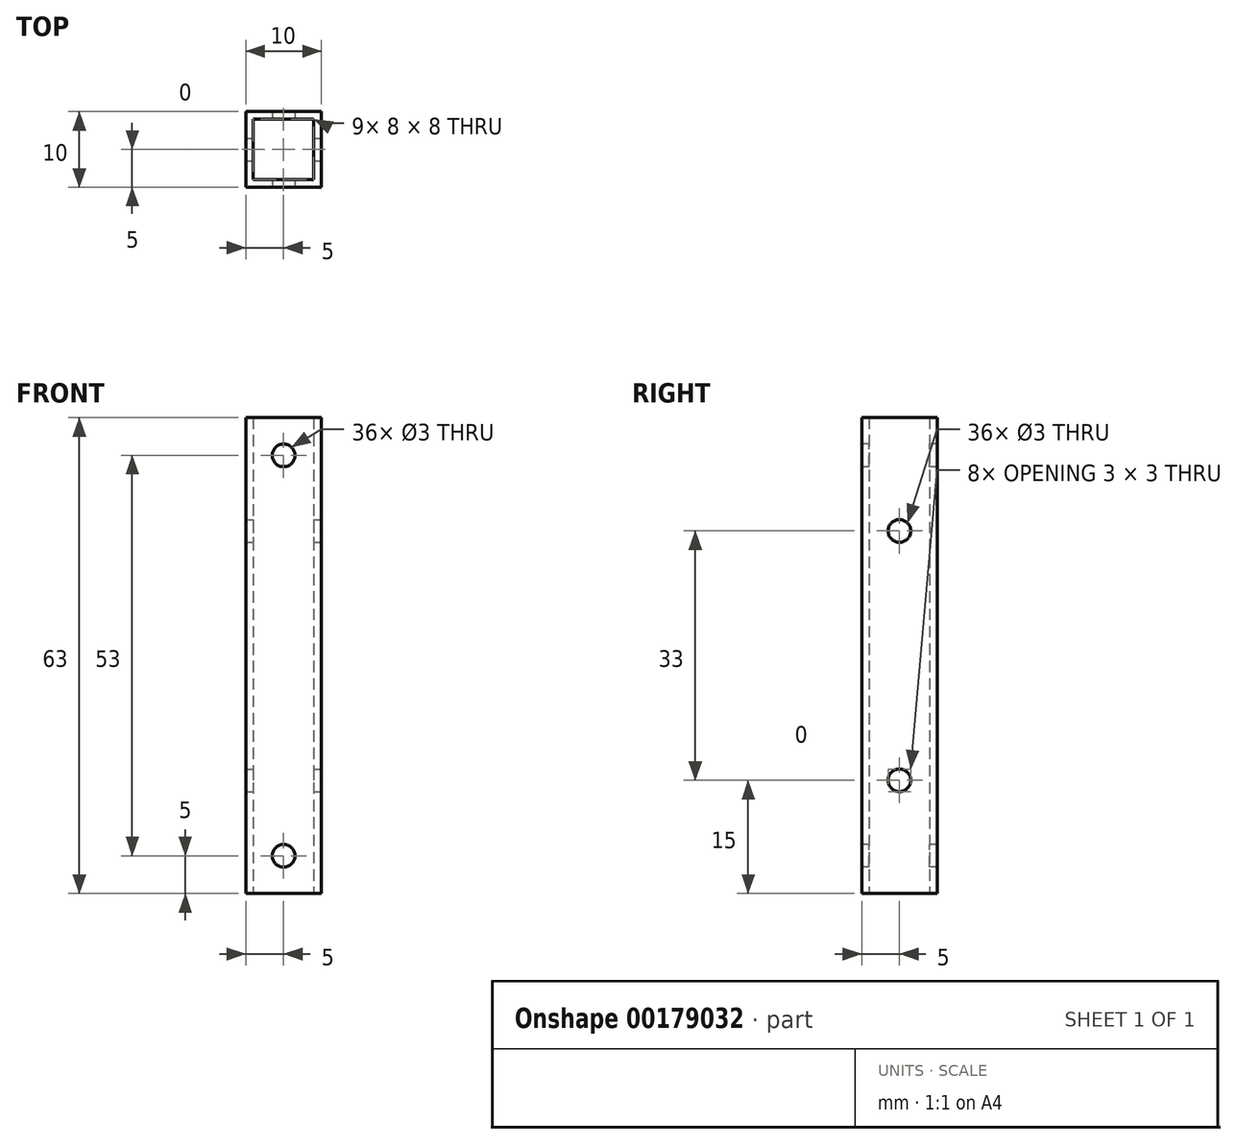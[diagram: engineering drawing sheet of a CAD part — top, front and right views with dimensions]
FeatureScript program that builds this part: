
annotation { "Feature Type Name" : "Feature", "Feature Type Description" : "" }
export const myFeature = defineFeature(function(context is Context, id is Id, definition is map)
    precondition{}
    {
        {
            var Q0;
            Q0=qCreatedBy(makeId("Top.planeOp"),FACE);
            var sketch = newSketch(context, id + "F0", { "sketchPlane" : qUnion([Q0])});
            skLineSegment(sketch, "E0.bottom", {"start": v(5, -5) * mm, "end": v(-5, -5) * mm});
            skLineSegment(sketch, "E0.top", {"start": v(5, 5) * mm, "end": v(-5, 5) * mm});
            skLineSegment(sketch, "E0.left", {"start": v(5, -5) * mm, "end": v(5, 5) * mm});
            skLineSegment(sketch, "E0.right", {"start": v(-5, -5) * mm, "end": v(-5, 5) * mm});
            skPoint(sketch, "E0.middle", {"position": v(0, 0) * mm});
            skLineSegment(sketch, "E1.bottom", {"start": v(4, -4) * mm, "end": v(-4, -4) * mm});
            skLineSegment(sketch, "E1.top", {"start": v(4, 4) * mm, "end": v(-4, 4) * mm});
            skLineSegment(sketch, "E1.left", {"start": v(4, -4) * mm, "end": v(4, 4) * mm});
            skLineSegment(sketch, "E1.right", {"start": v(-4, -4) * mm, "end": v(-4, 4) * mm});
            skSolve(sketch);
        }
        {
            var Q0;
            Q0 = qSketchRegion(id + "F0", true);
            extrude(context, id + "F1", {"entities" : qUnion([Q0]), "depth" : 63 * mm});
        }
        {
            var Q0;
            Q0=makeQuery(id+"F1.opExtrude","SWEPT_FACE",FACE,{"disambiguationData":[OSD([sQuery(id+"F0.wireOp",EDGE,"E0.bottom")])]});
            var sketch = newSketch(context, id + "F2", { "sketchPlane" : qUnion([Q0])});
            skLineSegment(sketch, "E2", {"start": v(0, 63) * mm, "end": v(0, 0) * mm, "construction": true});
            skLineSegment(sketch, "E3", {"start": v(-5, 31.5) * mm, "end": v(5, 31.5) * mm, "construction": true});
            skCircle(sketch, "E4", {"center": v(0, 5) * mm, "radius": 1.5 * mm});
            skCircle(sketch, "E5.MirrorC", {"center": v(0, 58) * mm, "radius": 1.5 * mm});
            skSolve(sketch);
        }
        {
            var Q0;
            Q0 = qSketchRegion(id + "F2", true);
            extrude(context, id + "F3", {"entities" : qUnion([Q0]), "operationType" : NewBodyOperationType.REMOVE, "oppositeDirection" : true, "depth" : 25 * mm});
        }
        {
            var Q0;
            Q0=makeQuery(id+"F1.opExtrude","SWEPT_FACE",FACE,{"disambiguationData":[OSD([sQuery(id+"F0.wireOp",EDGE,"E0.left")])]});
            var sketch = newSketch(context, id + "F4", { "sketchPlane" : qUnion([Q0])});
            skLineSegment(sketch, "E6", {"start": v(0, 63) * mm, "end": v(0, 0) * mm, "construction": true});
            skCircle(sketch, "E7", {"center": v(0, 48) * mm, "radius": 1.5 * mm});
            skLineSegment(sketch, "E8", {"start": v(-5, 31.5) * mm, "end": v(5, 31.5) * mm, "construction": true});
            skCircle(sketch, "E9.MirrorC", {"center": v(0, 15) * mm, "radius": 1.5 * mm});
            skSolve(sketch);
        }
        {
            var Q0;
            Q0 = qSketchRegion(id + "F4", true);
            extrude(context, id + "F5", {"entities" : qUnion([Q0]), "operationType" : NewBodyOperationType.REMOVE, "oppositeDirection" : true, "depth" : 25 * mm});
        }
    });
